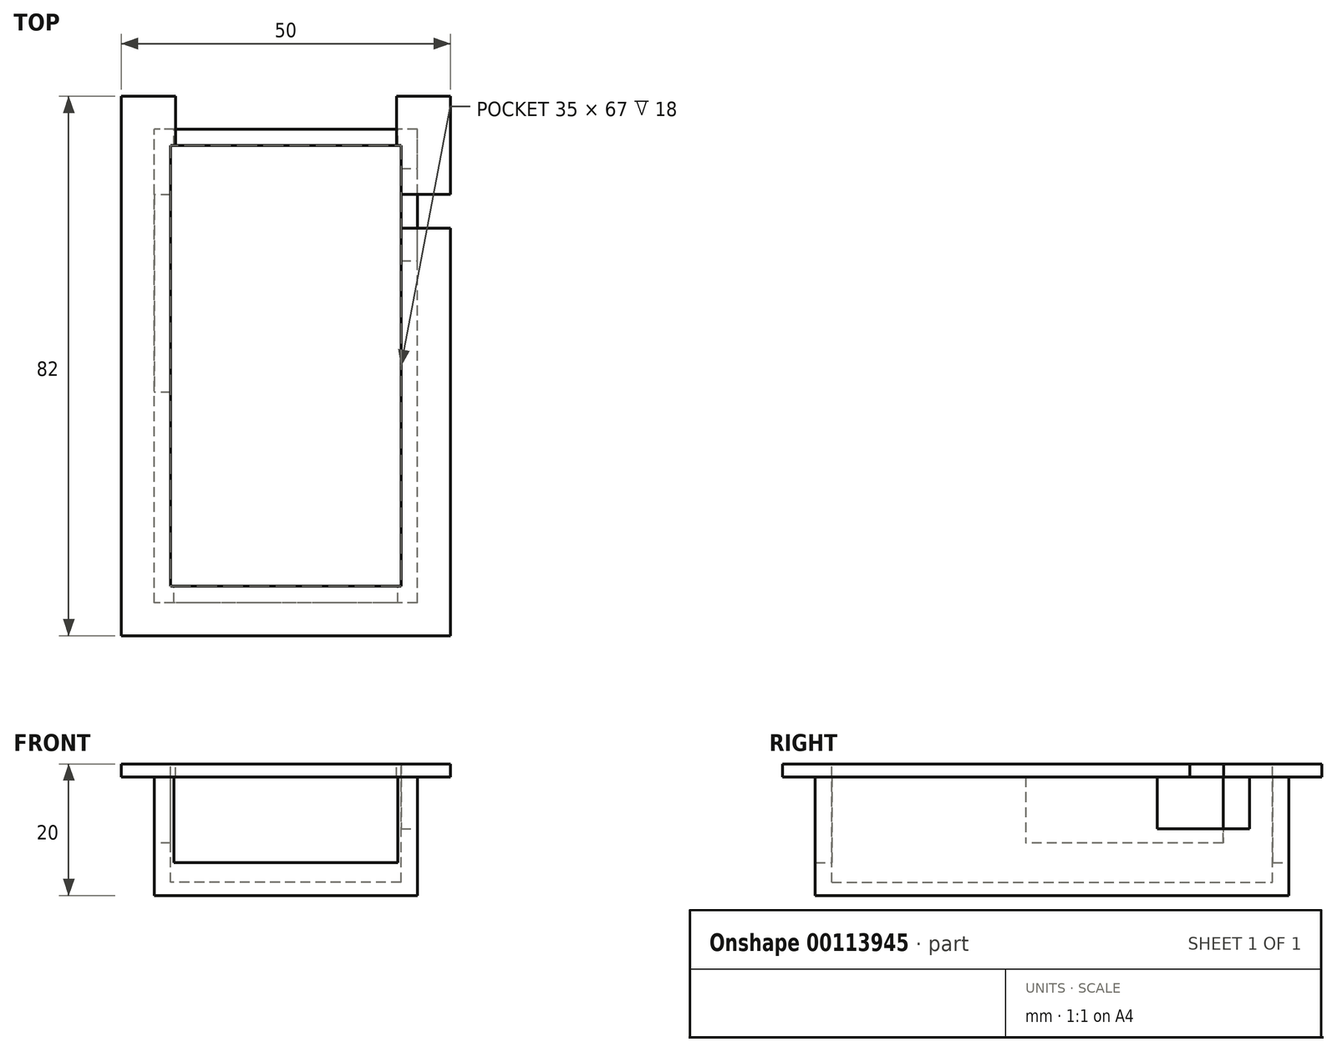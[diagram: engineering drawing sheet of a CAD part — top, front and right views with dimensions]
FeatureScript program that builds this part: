
annotation { "Feature Type Name" : "Feature", "Feature Type Description" : "" }
export const myFeature = defineFeature(function(context is Context, id is Id, definition is map)
    precondition{}
    {
        {
            var Q0;
            Q0=qCreatedBy(makeId("Top.planeOp"),FACE);
            var sketch = newSketch(context, id + "F0", { "sketchPlane" : qUnion([Q0])});
            skLineSegment(sketch, "E0.bottom", {"start": v(17.5, -33.5) * mm, "end": v(-17.5, -33.5) * mm});
            skLineSegment(sketch, "E0.top", {"start": v(17.5, 33.5) * mm, "end": v(-17.5, 33.5) * mm});
            skLineSegment(sketch, "E0.left", {"start": v(17.5, -33.5) * mm, "end": v(17.5, 33.5) * mm});
            skLineSegment(sketch, "E0.right", {"start": v(-17.5, -33.5) * mm, "end": v(-17.5, 33.5) * mm});
            skPoint(sketch, "E0.middle", {"position": v(0, 0) * mm});
            skLineSegment(sketch, "E1.0", {"start": v(20, 36) * mm, "end": v(-20, 36) * mm});
            skLineSegment(sketch, "E1.1", {"start": v(20, -36) * mm, "end": v(20, 36) * mm});
            skLineSegment(sketch, "E1.2", {"start": v(20, -36) * mm, "end": v(-20, -36) * mm});
            skLineSegment(sketch, "E1.3", {"start": v(-20, -36) * mm, "end": v(-20, 36) * mm});
            skLineSegment(sketch, "E2.0", {"start": v(-25, -41) * mm, "end": v(-25, 41) * mm});
            skLineSegment(sketch, "E2.1", {"start": v(25, -41) * mm, "end": v(-25, -41) * mm});
            skLineSegment(sketch, "E2.2", {"start": v(25, -41) * mm, "end": v(25, 41) * mm});
            skLineSegment(sketch, "E2.3", {"start": v(25, 41) * mm, "end": v(-25, 41) * mm});
            skSolve(sketch);
        }
        {
            var Q0;
            Q0=makeQuery(id+"F0.imprint","IMPRINT",FACE,{"disambiguationData":[TD([[makeQuery(id+"F0.imprint","IMPRINT",EDGE,{"derivedFrom":sQuery(id+"F0.wireOp",EDGE,"E0.bottom")}),1.0]])]});
            var Q1;
            Q1=makeQuery(id+"F0.imprint","IMPRINT",FACE,{"disambiguationData":[TD([[makeQuery(id+"F0.imprint","IMPRINT",EDGE,{"derivedFrom":sQuery(id+"F0.wireOp",EDGE,"E0.bottom")}),-1.0]])]});
            extrude(context, id + "F1", {"entities" : qUnion([Q0, Q1]), "oppositeDirection" : true, "depth" : 20 * mm});
        }
        {
            var Q0;
            Q0 = qSketchRegion(id + "F0", true);
            extrude(context, id + "F2", {"entities" : qUnion([Q0]), "operationType" : NewBodyOperationType.ADD, "oppositeDirection" : true, "depth" : 2 * mm});
        }
        {
            var Q0;
            Q0=makeQuery(id+"F0.imprint","IMPRINT",FACE,{"disambiguationData":[TD([[makeQuery(id+"F0.imprint","IMPRINT",EDGE,{"derivedFrom":sQuery(id+"F0.wireOp",EDGE,"E0.bottom")}),-1.0]])]});
            extrude(context, id + "F3", {"entities" : qUnion([Q0]), "operationType" : NewBodyOperationType.REMOVE, "oppositeDirection" : true, "depth" : 18 * mm});
        }
        {
            var Q0;
            Q0=makeQuery(id+"F1.opExtrude","SWEPT_FACE",FACE,{"disambiguationData":[OSD([sQuery(id+"F0.wireOp",EDGE,"E1.1")])]});
            var sketch = newSketch(context, id + "F4", { "sketchPlane" : qUnion([Q0])});
            skLineSegment(sketch, "E3.bottom", {"start": v(16, -2) * mm, "end": v(30, -2) * mm});
            skLineSegment(sketch, "E3.top", {"start": v(16, -9.84) * mm, "end": v(30, -9.84) * mm});
            skLineSegment(sketch, "E3.left", {"start": v(16, -2) * mm, "end": v(16, -9.84) * mm});
            skLineSegment(sketch, "E3.right", {"start": v(30, -2) * mm, "end": v(30, -9.84) * mm});
            skPoint(sketch, "E3.middle", {"position": v(23, -5.92) * mm});
            skSolve(sketch);
        }
        {
            var Q0;
            Q0=makeQuery(id+"F4.imprint","IMPRINT",FACE,{"disambiguationData":[TD([[makeQuery(id+"F4.imprint","IMPRINT",EDGE,{"derivedFrom":sQuery(id+"F4.wireOp",EDGE,"E3.bottom")}),-1.0]])]});
            extrude(context, id + "F5", {"entities" : qUnion([Q0]), "operationType" : NewBodyOperationType.REMOVE, "oppositeDirection" : true, "depth" : 5 * mm});
        }
        {
            var Q0;
            Q0=makeQuery(id+"F1.opExtrude","SWEPT_FACE",FACE,{"disambiguationData":[OSD([sQuery(id+"F0.wireOp",EDGE,"E1.3")])]});
            var sketch = newSketch(context, id + "F6", { "sketchPlane" : qUnion([Q0])});
            skLineSegment(sketch, "E4.bottom", {"start": v(-26, -2) * mm, "end": v(4, -2) * mm});
            skLineSegment(sketch, "E4.top", {"start": v(-26, -12) * mm, "end": v(4, -12) * mm});
            skLineSegment(sketch, "E4.left", {"start": v(-26, -2) * mm, "end": v(-26, -12) * mm});
            skLineSegment(sketch, "E4.right", {"start": v(4, -2) * mm, "end": v(4, -12) * mm});
            skSolve(sketch);
        }
        {
            var Q0;
            Q0=makeQuery(id+"F6.imprint","IMPRINT",FACE,{"disambiguationData":[TD([[makeQuery(id+"F6.imprint","IMPRINT",EDGE,{"derivedFrom":sQuery(id+"F6.wireOp",EDGE,"E4.bottom")}),1.0]])]});
            extrude(context, id + "F7", {"entities" : qUnion([Q0]), "operationType" : NewBodyOperationType.REMOVE, "oppositeDirection" : true, "depth" : 5 * mm});
        }
        {
            var Q0;
            Q0=makeQuery(id+"F1.opExtrude","SWEPT_FACE",FACE,{"disambiguationData":[OSD([sQuery(id+"F0.wireOp",EDGE,"E1.0")])]});
            var sketch = newSketch(context, id + "F8", { "sketchPlane" : qUnion([Q0])});
            skLineSegment(sketch, "E5.bottom", {"start": v(-17, -2) * mm, "end": v(17, -2) * mm});
            skLineSegment(sketch, "E5.top", {"start": v(-17, -15) * mm, "end": v(17, -15) * mm});
            skLineSegment(sketch, "E5.left", {"start": v(-17, -2) * mm, "end": v(-17, -15) * mm});
            skLineSegment(sketch, "E5.right", {"start": v(17, -2) * mm, "end": v(17, -15) * mm});
            skSolve(sketch);
        }
        {
            var Q0;
            Q0=makeQuery(id+"F8.imprint","IMPRINT",FACE,{"disambiguationData":[TD([[makeQuery(id+"F8.imprint","IMPRINT",EDGE,{"derivedFrom":sQuery(id+"F8.wireOp",EDGE,"E5.bottom")}),-1.0]])]});
            extrude(context, id + "F9", {"entities" : qUnion([Q0]), "operationType" : NewBodyOperationType.REMOVE, "oppositeDirection" : true, "depth" : 126.25 * mm});
        }
        {
            var Q0;
            Q0=makeQuery(id+"F0.imprint","IMPRINT",FACE,{"disambiguationData":[TD([[makeQuery(id+"F0.imprint","IMPRINT",EDGE,{"derivedFrom":sQuery(id+"F0.wireOp",EDGE,"E1.0")}),-1.0]])]});
            var sketch = newSketch(context, id + "F10", { "sketchPlane" : qUnion([Q0])});
            skLineSegment(sketch, "E6.bottom", {"start": v(13.85, 26.07) * mm, "end": v(25.03, 26.07) * mm});
            skLineSegment(sketch, "E6.top", {"start": v(13.85, 20.93) * mm, "end": v(25.03, 20.93) * mm});
            skLineSegment(sketch, "E6.left", {"start": v(13.85, 26.07) * mm, "end": v(13.85, 20.93) * mm});
            skLineSegment(sketch, "E6.right", {"start": v(25.03, 26.07) * mm, "end": v(25.03, 20.93) * mm});
            skLineSegment(sketch, "E7.bottom", {"start": v(16.83, 44.65) * mm, "end": v(-16.8, 44.65) * mm});
            skLineSegment(sketch, "E7.top", {"start": v(16.83, 31.36) * mm, "end": v(-16.8, 31.36) * mm});
            skLineSegment(sketch, "E7.left", {"start": v(16.83, 44.65) * mm, "end": v(16.83, 31.36) * mm});
            skLineSegment(sketch, "E7.right", {"start": v(-16.8, 44.65) * mm, "end": v(-16.8, 31.36) * mm});
            skSolve(sketch);
        }
        {
            var Q0;
            {var subQ0=sQuery(id+"F10.wireOp",EDGE,"E6.bottom");var subQ1=makeQuery(id+"F0.imprint","IMPRINT",EDGE,{"derivedFrom":sQuery(id+"F0.wireOp",EDGE,"E2.2")});var subQ2=makeQuery(id+"F10.imprint","INTERSECT",VERTEX,{"derivedFrom":[subQ1,subQ0]});Q0=makeQuery(id+"F10.imprint","IMPRINT",FACE,{"disambiguationData":[TD([[makeQuery(id+"F10.imprint","IMPRINT",EDGE,{"disambiguationData":[TD([[subQ2,1.0]])],"derivedFrom":subQ0}),-1.0]])]});}
            var Q1;
            {var subQ0=sQuery(id+"F10.wireOp",EDGE,"E7.left");var subQ1=makeQuery(id+"F0.imprint","IMPRINT",EDGE,{"derivedFrom":sQuery(id+"F0.wireOp",EDGE,"E2.3")});var subQ2=makeQuery(id+"F10.imprint","INTERSECT",VERTEX,{"derivedFrom":[subQ1,subQ0]});Q1=makeQuery(id+"F10.imprint","IMPRINT",FACE,{"disambiguationData":[TD([[makeQuery(id+"F10.imprint","IMPRINT",EDGE,{"disambiguationData":[TD([[subQ2,-1.0]])],"derivedFrom":subQ0}),-1.0]])]});}
            var Q2;
            {var subQ0=sQuery(id+"F10.wireOp",EDGE,"E7.top");Q2=makeQuery(id+"F10.imprint","IMPRINT",FACE,{"disambiguationData":[TD([[makeQuery(id+"F10.imprint","IMPRINT",EDGE,{"derivedFrom":subQ0}),-1.0]])]});}
            var Q3;
            {var subQ0=sQuery(id+"F10.wireOp",EDGE,"E6.left");Q3=makeQuery(id+"F10.imprint","IMPRINT",FACE,{"disambiguationData":[TD([[makeQuery(id+"F10.imprint","IMPRINT",EDGE,{"derivedFrom":subQ0}),1.0]])]});}
            extrude(context, id + "F11", {"entities" : qUnion([Q0, Q1, Q2, Q3]), "operationType" : NewBodyOperationType.REMOVE, "oppositeDirection" : true, "depth" : 5 * mm});
        }
    });
